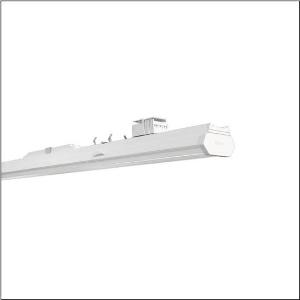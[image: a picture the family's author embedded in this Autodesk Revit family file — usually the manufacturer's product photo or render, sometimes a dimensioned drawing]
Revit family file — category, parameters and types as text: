
# Revit family: licross_r__11_protected_mo_51tp11mn495g_eae0
name_source: partatom
category: Lighting Fixtures
units: mm (PartAtom-declared; Revit-internal decimal feet)

## family parameters
Cut with Voids When Loaded = No
Host = Face
Light Source = No
Part Type = Normal
Room Calculation Point = No
Round Connector Dimension = Use Diameter
Shared = No

## types (1)
- --- (1 x LED, 9980 lm, 55.3 W, 4000K)
    Apparent Load = 55 VA
    CIE Flux Codes = 83 94 98 100 100
    Color Rendering = 80
    Color Temperature = 4000K
    Default Elevation = 1800 mm
    Description = Licross® 11 Protected MO, luminaire insert, of sheet steel, galvanised, coil coated, white, length: 1.500mm, width: 90mm, height: 101mm, LED rated luminous flux: 9.980lm, light colour: 840, control gear: ON/OFF Multilumen, with plug, 3-pole, with phase selection, mains connection: 220..240V, AC, 50/60Hz, rated input power: 55W, halogen-free wiring, primary light control with lens, of plastic, primary optical cover: cover, of PMMA, light emission: direct distribution, primary light characteristic: symmetric, protection rating (complete): IP64, insulation class (complete): insulation class I (protective earthing), certification: CE, ENEC, VDE, UKCA, protection symbol: D if used in an environment with conductive dust loads with corresponding accessories, impact resistance: IK06, permissible ambient temperature for indoor applications: -35..+40°C, corresponds to IFS (International Featured Standards) requirements for safety and quality in the food industry, reducing of maximum allowable ambient temperature of 5°C with ceiling mounting, LABS conformity tested according to VDMA 24364:2018-05, packaging unit: 1 piece
    Height = 92 mm
    Lamp = 1 x LED
    Lamp Light Flux = 9980 lm
    Lamp Power = 55.3 W
    Lamp count = 1
    Length = 1500 mm
    Luminous efficacy = 180 lm/W
    Manufacturer = Siteco
    ModVariant = No
    Model = 51TP11MN495G
    Mounting Place = Ceiling
    Mounting Type = Pendant
    Number of Poles = 1
    OnlyDefault = Yes
    Power Factor = 1
    Product Name = Licross® 11 Protected MO
    Product group = luminaire insert
    ProductGroupID = 901
    Protection Class = Protection class I
    Protection Degree = IP 64
    RLX_Detail_Level = 1
    RLX_Emergency_Light_Flux = 0 lm
    RLX_Emergency_Type = 0
    RLX_Emergency_Type_DB = No
    RlxData = <blob elided: 21849 chars, md5=f634e378>
    Socket = socket
    Standby Power = 0 W
    System Light Flux = 9980 lm
    System Power = 55 W
    Type Comments = factory setting: luminous flux: 100 % | (A | C | E) | 126 mA
    Type Image = l_1256148.jpg
    URL = http://relux.com
    VarID = @adj_037975
    Voltage = 0 V
    Weight = 0.00 kg
    Width = 88 mm

## geometry (parser evidence)
native form markers: Blend x4, Sweep x12
no freeform markers — native parametric forms only
